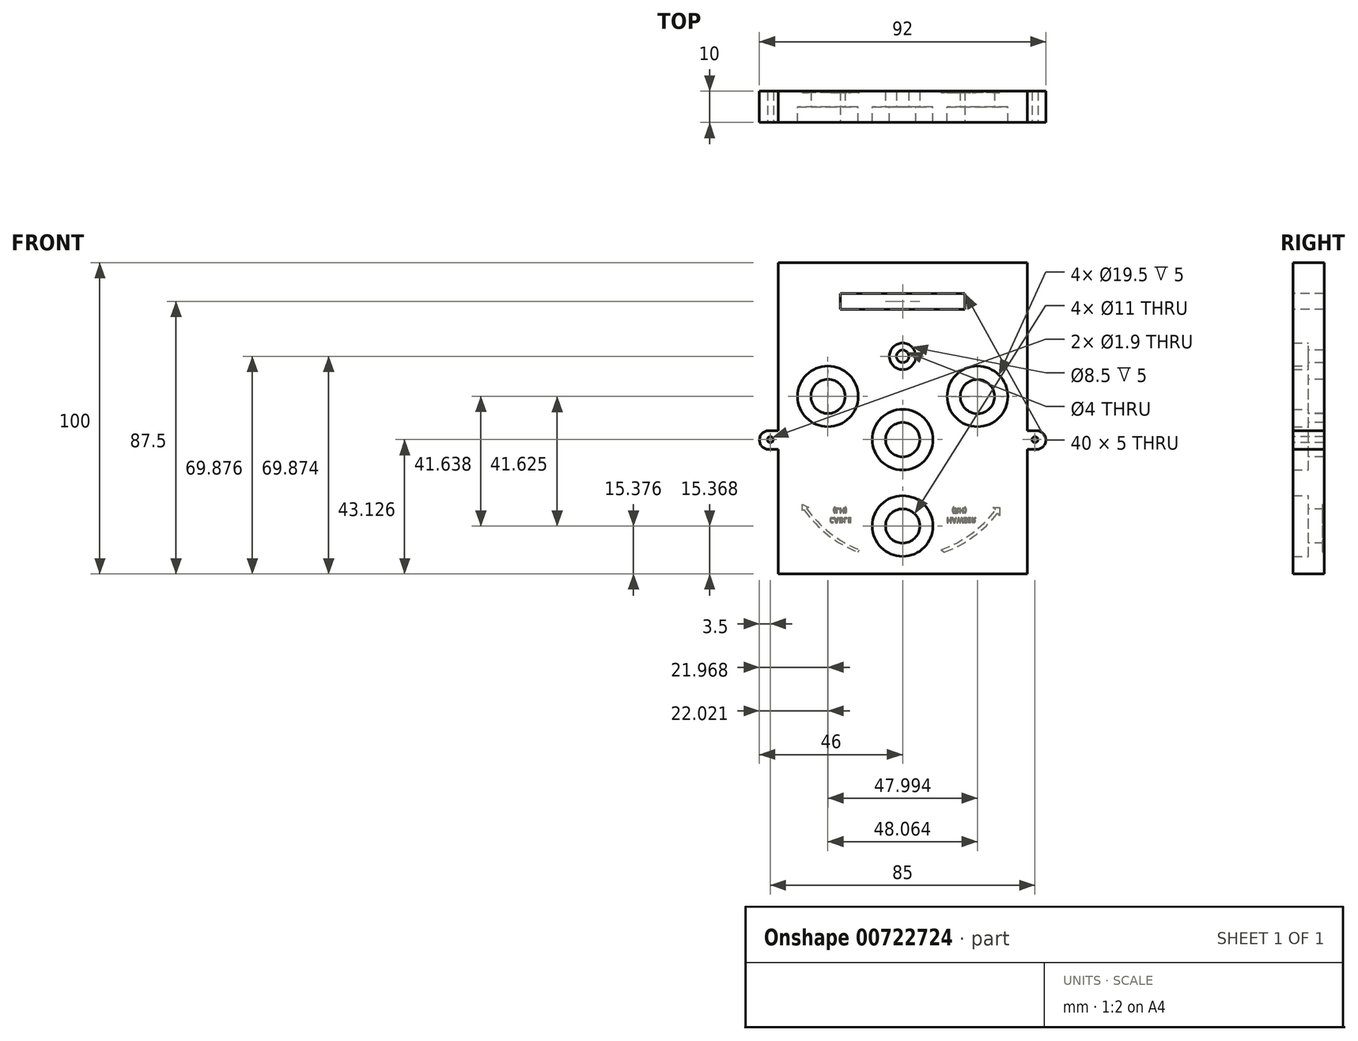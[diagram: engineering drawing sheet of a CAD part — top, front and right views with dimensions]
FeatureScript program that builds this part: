
annotation { "Feature Type Name" : "Feature", "Feature Type Description" : "" }
export const myFeature = defineFeature(function(context is Context, id is Id, definition is map)
    precondition{}
    {
        {
            var Q0;
            Q0=qCreatedBy(makeId("Front.planeOp"),FACE);
            var sketch = newSketch(context, id + "F0", { "sketchPlane" : qUnion([Q0])});
            skLineSegment(sketch, "E0.bottom", {"start": v(-40, 60) * mm, "end": v(40, 60) * mm});
            skLineSegment(sketch, "E0.top", {"start": v(-40, -60) * mm, "end": v(40, -60) * mm});
            skLineSegment(sketch, "E0.left", {"start": v(-40, 60) * mm, "end": v(-40, -60) * mm});
            skLineSegment(sketch, "E0.right", {"start": v(40, 60) * mm, "end": v(40, -60) * mm});
            skPoint(sketch, "E0.middle", {"position": v(0, 0) * mm});
            skLineSegment(sketch, "E1", {"start": v(0, 21.88) * mm, "end": v(0, 29.88) * mm, "construction": true});
            skCircle(sketch, "E2", {"center": v(0, 29.88) * mm, "radius": 8 * mm, "construction": true});
            skCircle(sketch, "E3", {"center": v(0, 29.88) * mm, "radius": 4.25 * mm});
            skLineSegment(sketch, "E4", {"start": v(0, 60) * mm, "end": v(0, 29.88) * mm, "construction": true});
            skLineSegment(sketch, "E5", {"start": v(0, 21.88) * mm, "end": v(0, 3.13) * mm, "construction": true});
            skCircle(sketch, "E6", {"center": v(0, 3.13) * mm, "radius": 18.75 * mm, "construction": true});
            skCircle(sketch, "E7.cCircle", {"center": v(0, 3.13) * mm, "radius": 27.75 * mm, "construction": true});
            skLineSegment(sketch, "E7.0", {"start": v(0, -24.62) * mm, "end": v(-24.03, 17) * mm, "construction": true});
            skLineSegment(sketch, "E7.1", {"start": v(-24.03, 17) * mm, "end": v(24.03, 17) * mm, "construction": true});
            skLineSegment(sketch, "E7.2", {"start": v(24.03, 17) * mm, "end": v(0, -24.62) * mm, "construction": true});
            skCircle(sketch, "E8", {"center": v(24.03, 17) * mm, "radius": 8 * mm, "construction": true});
            skCircle(sketch, "E9", {"center": v(-24.03, 17) * mm, "radius": 8 * mm, "construction": true});
            skCircle(sketch, "E10", {"center": v(0, -24.62) * mm, "radius": 8 * mm, "construction": true});
            skCircle(sketch, "E11", {"center": v(0, 3.13) * mm, "radius": 9.75 * mm});
            skCircle(sketch, "E12", {"center": v(24.03, 17) * mm, "radius": 9.75 * mm});
            skCircle(sketch, "E13", {"center": v(-24.03, 17) * mm, "radius": 9.75 * mm});
            skCircle(sketch, "E14", {"center": v(0, -24.62) * mm, "radius": 9.75 * mm});
            skSolve(sketch);
        }
        {
            var Q0;
            Q0=qSketchRegion(id+"F0",true);
            extrude(context, id + "F1", {"entities" : qUnion([Q0]), "depth" : 5 * mm, "offsetDistance" : 25 * mm});
        }
        {
            var Q0;
            Q0=qCreatedBy(makeId("Front.planeOp"),FACE);
            var sketch = newSketch(context, id + "F2", { "sketchPlane" : qUnion([Q0])});
            skLineSegment(sketch, "E15.bottom", {"start": v(40, -60) * mm, "end": v(-40, -60) * mm});
            skLineSegment(sketch, "E15.top", {"start": v(40, 60) * mm, "end": v(-40, 60) * mm});
            skLineSegment(sketch, "E15.left", {"start": v(40, -60) * mm, "end": v(40, 60) * mm});
            skLineSegment(sketch, "E15.right", {"start": v(-40, -60) * mm, "end": v(-40, 60) * mm});
            skPoint(sketch, "E15.middle", {"position": v(0, 0) * mm});
            skCircle(sketch, "E16", {"center": v(0, 3.12) * mm, "radius": 5.5 * mm});
            skCircle(sketch, "E17", {"center": v(0, -24.63) * mm, "radius": 5.5 * mm});
            skCircle(sketch, "E18", {"center": v(24.02, 16.94) * mm, "radius": 5.5 * mm});
            skCircle(sketch, "E19", {"center": v(-23.98, 17) * mm, "radius": 5.5 * mm});
            skCircle(sketch, "E20", {"center": v(0, 29.87) * mm, "radius": 2 * mm});
            skSolve(sketch);
        }
        {
            var Q0;
            Q0=qSketchRegion(id+"F2",true);
            extrude(context, id + "F3", {"entities" : qUnion([Q0]), "operationType" : NewBodyOperationType.ADD, "oppositeDirection" : true, "depth" : 5 * mm, "offsetDistance" : 25 * mm});
        }
        {
            var Q0;
            Q0=makeQuery(id+"F1.opExtrude","CAP_FACE",FACE,{"disambiguationData":[OSD([sQuery(id+"F0.wireOp",EDGE,"E0.bottom"),sQuery(id+"F0.wireOp",EDGE,"E0.top"),sQuery(id+"F0.wireOp",EDGE,"E0.left"),sQuery(id+"F0.wireOp",EDGE,"E0.right"),sQuery(id+"F0.wireOp",EDGE,"E11"),sQuery(id+"F0.wireOp",EDGE,"E3"),sQuery(id+"F0.wireOp",EDGE,"E12"),sQuery(id+"F0.wireOp",EDGE,"E13"),sQuery(id+"F0.wireOp",EDGE,"E14")])],"isStart":false});
            var sketch = newSketch(context, id + "F4", { "sketchPlane" : qUnion([Q0])});
            skLineSegment(sketch, "E21.bottom", {"start": v(40, -60) * mm, "end": v(-40, -60) * mm});
            skLineSegment(sketch, "E21.top", {"start": v(40, -40) * mm, "end": v(-40, -40) * mm});
            skLineSegment(sketch, "E21.left", {"start": v(40, -60) * mm, "end": v(40, -40) * mm});
            skLineSegment(sketch, "E21.right", {"start": v(-40, -60) * mm, "end": v(-40, -40) * mm});
            skSolve(sketch);
        }
        {
            var Q0;
            Q0=qSketchRegion(id+"F4",true);
            extrude(context, id + "F5", {"entities" : qUnion([Q0]), "operationType" : NewBodyOperationType.REMOVE, "oppositeDirection" : true, "depth" : 10 * mm, "offsetDistance" : 25 * mm});
        }
        {
            var Q0;
            Q0=makeQuery(id+"F1.opExtrude","CAP_FACE",FACE,{"disambiguationData":[OSD([sQuery(id+"F0.wireOp",EDGE,"E0.bottom"),sQuery(id+"F0.wireOp",EDGE,"E0.top"),sQuery(id+"F0.wireOp",EDGE,"E0.left"),sQuery(id+"F0.wireOp",EDGE,"E0.right"),sQuery(id+"F0.wireOp",EDGE,"E11"),sQuery(id+"F0.wireOp",EDGE,"E3"),sQuery(id+"F0.wireOp",EDGE,"E12"),sQuery(id+"F0.wireOp",EDGE,"E13"),sQuery(id+"F0.wireOp",EDGE,"E14")])],"isStart":false});
            var sketch = newSketch(context, id + "F6", { "sketchPlane" : qUnion([Q0])});
            skLineSegment(sketch, "E22", {"start": v(0, 3.13) * mm, "end": v(42.5, 3.13) * mm, "construction": true});
            skLineSegment(sketch, "E23", {"start": v(42.5, 3.13) * mm, "end": v(42.5, 0.13) * mm, "construction": true});
            skLineSegment(sketch, "E24.bottom", {"start": v(40, 0) * mm, "end": v(46, 0) * mm});
            skLineSegment(sketch, "E24.top", {"start": v(40, 6) * mm, "end": v(46, 6) * mm});
            skLineSegment(sketch, "E24.left", {"start": v(40, 0) * mm, "end": v(40, 6) * mm});
            skLineSegment(sketch, "E24.right", {"start": v(46, 0) * mm, "end": v(46, 6) * mm});
            skCircle(sketch, "E25", {"center": v(42.5, 3.13) * mm, "radius": 0.95 * mm});
            skSolve(sketch);
        }
        {
            var Q0;
            Q0=qSketchRegion(id+"F6",true);
            extrude(context, id + "F7", {"entities" : qUnion([Q0]), "oppositeDirection" : true, "depth" : 10 * mm, "offsetDistance" : 25 * mm});
        }
        {
            var Q0;
            Q0=makeQuery(id+"F7.opExtrude","SWEPT_EDGE",EDGE,{"disambiguationData":[OSD([sQuery(id+"F6.wireOp",EDGE,"E24.bottom"),sQuery(id+"F6.wireOp",EDGE,"E24.right")])]});
            var Q1;
            Q1=makeQuery(id+"F7.opExtrude","SWEPT_EDGE",EDGE,{"disambiguationData":[OSD([sQuery(id+"F6.wireOp",EDGE,"E24.top"),sQuery(id+"F6.wireOp",EDGE,"E24.right")])]});
            fillet(context, id + "F8", {"entities" : qUnion([Q0, Q1]), "radius" : 3 * mm, "tangentPropagation" : true, "allowEdgeOverflow" : false});
        }
        {
            var Q0;
            Q0=makeQuery(id+"F7.opExtrude","SWEPT_BODY",BODY,{"disambiguationData":[OSD([sQuery(id+"F6.wireOp",EDGE,"E24.bottom"),sQuery(id+"F6.wireOp",EDGE,"E24.top"),sQuery(id+"F6.wireOp",EDGE,"E24.left"),sQuery(id+"F6.wireOp",EDGE,"E24.right"),sQuery(id+"F6.wireOp",EDGE,"E25")])]});
            var Q1;
            Q1=qCreatedBy(makeId("Right.planeOp"),FACE);
            mirror(context, id + "F9", {"operationType" : NewBodyOperationType.ADD, "entities" : qUnion([Q0]), "mirrorPlane" : qUnion([Q1])});
        }
        {
            var Q0;
            Q0=makeQuery(id+"F1.opExtrude","CAP_FACE",FACE,{"disambiguationData":[OSD([sQuery(id+"F0.wireOp",EDGE,"E0.bottom"),sQuery(id+"F0.wireOp",EDGE,"E0.top"),sQuery(id+"F0.wireOp",EDGE,"E0.left"),sQuery(id+"F0.wireOp",EDGE,"E0.right"),sQuery(id+"F0.wireOp",EDGE,"BUhoPo5e-iJjO-Hz3U-B1AJ-PJeumMdkG3JQ"),sQuery(id+"F0.wireOp",EDGE,"E3"),sQuery(id+"F0.wireOp",EDGE,"iMyCUadU-kSq6-7gJk-bGzv-rUmCgOXwhL5P"),sQuery(id+"F0.wireOp",EDGE,"g6cQsEgE-VhaZ-rvnu-1JBG-t1yHCIxkASWM"),sQuery(id+"F0.wireOp",EDGE,"NTCEa5vw-s6QI-k5br-llQC-EMKQmXEYU9zL")])],"isStart":false});
            var sketch = newSketch(context, id + "F11", { "sketchPlane" : qUnion([Q0])});
            skLineSegment(sketch, "E26", {"start": v(40, 60) * mm, "end": v(20, 60) * mm, "construction": true});
            skLineSegment(sketch, "E27", {"start": v(20, 60) * mm, "end": v(20, 50) * mm, "construction": true});
            skLineSegment(sketch, "E28.bottom", {"start": v(20, 50) * mm, "end": v(-20, 50) * mm});
            skLineSegment(sketch, "E28.top", {"start": v(20, 45) * mm, "end": v(-20, 45) * mm});
            skLineSegment(sketch, "E28.left", {"start": v(20, 50) * mm, "end": v(20, 45) * mm});
            skLineSegment(sketch, "E28.right", {"start": v(-20, 50) * mm, "end": v(-20, 45) * mm});
            skSolve(sketch);
        }
        {
            var Q0;
            Q0=qSketchRegion(id+"F11",true);
            extrude(context, id + "F12", {"entities" : qUnion([Q0]), "operationType" : NewBodyOperationType.REMOVE, "oppositeDirection" : true, "depth" : 10 * mm, "offsetDistance" : 25 * mm, "hasSecondDirection" : true, "secondDirectionOppositeDirection" : false, "secondDirectionDepth" : 2 * mm});
        }
        {
            var Q0;
            {var subQ0=makeQuery(id+"F7.opExtrude","CAP_FACE",FACE,{"disambiguationData":[OSD([sQuery(id+"F6.wireOp",EDGE,"E24.bottom"),sQuery(id+"F6.wireOp",EDGE,"E24.top"),sQuery(id+"F6.wireOp",EDGE,"E24.left"),sQuery(id+"F6.wireOp",EDGE,"E24.right"),sQuery(id+"F6.wireOp",EDGE,"E25")])],"isStart":false});Q0=makeQuery(id+"F9.boolean.opBoolean","MERGE",FACE,{"derivedFrom":[makeQuery(id+"F3.opExtrude","CAP_FACE",FACE,{"disambiguationData":[OSD([sQuery(id+"F2.wireOp",EDGE,"E15.bottom"),sQuery(id+"F2.wireOp",EDGE,"E15.top"),sQuery(id+"F2.wireOp",EDGE,"E15.left"),sQuery(id+"F2.wireOp",EDGE,"E15.right"),sQuery(id+"F2.wireOp",EDGE,"E16"),sQuery(id+"F2.wireOp",EDGE,"E17"),sQuery(id+"F2.wireOp",EDGE,"E18"),sQuery(id+"F2.wireOp",EDGE,"E19"),sQuery(id+"F2.wireOp",EDGE,"E20")])],"isStart":false}),subQ0,makeQuery(id+"F9.opPattern","COPY",FACE,{"derivedFrom":subQ0,"instanceName":"1"})]});}
            var sketch = newSketch(context, id + "F13", { "sketchPlane" : qUnion([Q0])});
            skArc(sketch, "E29", {"start": v(14.26, -33.06) * mm, "mid": v(23.94, -27.53) * mm, "end": v(31.65, -19.48) * mm});
            skArc(sketch, "E30", {"start": v(13.93, -32.23) * mm, "mid": v(23.4, -26.82) * mm, "end": v(30.94, -18.94) * mm});
            skArc(sketch, "E31", {"start": v(-13.38, -33.06) * mm, "mid": v(-22.83, -27.98) * mm, "end": v(-30.51, -20.48) * mm});
            skArc(sketch, "E32", {"start": v(-12.33, -32.23) * mm, "mid": v(-22.03, -27.15) * mm, "end": v(-29.85, -19.48) * mm});
            skLineSegment(sketch, "E33", {"start": v(14.26, -33.06) * mm, "end": v(13.93, -32.23) * mm});
            skLineSegment(sketch, "E34", {"start": v(-12.33, -32.23) * mm, "end": v(-13.38, -33.06) * mm});
            skLineSegment(sketch, "E35.2", {"start": v(28.49, -20.51) * mm, "end": v(28.49, -20.51) * mm});
            skPoint(sketch, "E35.0.midPoint", {"position": v(31.65, -20.51) * mm});
            skPoint(sketch, "E35.cCircle.center.orphan", {"position": v(31.65, -18.69) * mm});
            skPoint(sketch, "E36.orphan", {"position": v(34.82, -20.51) * mm});
            skLineSegment(sketch, "E37", {"start": v(31.65, -19.48) * mm, "end": v(32.26, -19.73) * mm});
            skLineSegment(sketch, "E38", {"start": v(32.26, -19.73) * mm, "end": v(32.26, -17.7) * mm});
            skLineSegment(sketch, "E39", {"start": v(32.26, -17.7) * mm, "end": v(30.18, -18.62) * mm});
            skLineSegment(sketch, "E40", {"start": v(30.18, -18.62) * mm, "end": v(30.94, -18.94) * mm});
            skPoint(sketch, "E41.trimOffspring.end.orphan", {"position": v(31.65, -17.9) * mm});
            skLineSegment(sketch, "E42", {"start": v(-29.85, -19.48) * mm, "end": v(-29.05, -18.72) * mm});
            skLineSegment(sketch, "E43", {"start": v(-29.05, -18.72) * mm, "end": v(-31.2, -18.72) * mm});
            skLineSegment(sketch, "E44", {"start": v(-31.2, -18.72) * mm, "end": v(-31.2, -21.32) * mm});
            skLineSegment(sketch, "E45", {"start": v(-31.2, -21.32) * mm, "end": v(-30.51, -20.48) * mm});
            skSolve(sketch);
        }
        {
            var Q0;
            Q0 = qSketchRegion(id + "F13", true);
            extrude(context, id + "F14", {"entities" : qUnion([Q0]), "operationType" : NewBodyOperationType.REMOVE, "oppositeDirection" : true, "depth" : 0.4 * mm, "offsetDistance" : 25 * mm});
        }
        {
            var Q0;
            {var subQ0=makeQuery(id+"F7.opExtrude","CAP_FACE",FACE,{"disambiguationData":[OSD([sQuery(id+"F6.wireOp",EDGE,"E24.bottom"),sQuery(id+"F6.wireOp",EDGE,"E24.top"),sQuery(id+"F6.wireOp",EDGE,"E24.left"),sQuery(id+"F6.wireOp",EDGE,"E24.right"),sQuery(id+"F6.wireOp",EDGE,"E25")])],"isStart":false});Q0=makeQuery(id+"F9.boolean.opBoolean","MERGE",FACE,{"derivedFrom":[makeQuery(id+"F3.opExtrude","CAP_FACE",FACE,{"disambiguationData":[OSD([sQuery(id+"F2.wireOp",EDGE,"E15.bottom"),sQuery(id+"F2.wireOp",EDGE,"E15.top"),sQuery(id+"F2.wireOp",EDGE,"E15.left"),sQuery(id+"F2.wireOp",EDGE,"E15.right"),sQuery(id+"F2.wireOp",EDGE,"E16"),sQuery(id+"F2.wireOp",EDGE,"E17"),sQuery(id+"F2.wireOp",EDGE,"E18"),sQuery(id+"F2.wireOp",EDGE,"E19"),sQuery(id+"F2.wireOp",EDGE,"E20")])],"isStart":false}),subQ0,makeQuery(id+"F9.opPattern","COPY",FACE,{"derivedFrom":subQ0,"instanceName":"1"})]});}
            var sketch = newSketch(context, id + "F15", { "sketchPlane" : qUnion([Q0])});
            skText(sketch, "E46", { "text": "HAWSER\n   (RH)", "fontName": "OpenSans-Bold.ttf"});
            skText(sketch, "E47", { "text": "CABLE\n  (LH)", "fontName": "OpenSans-Bold.ttf"});
            const initialGuessF15  = {"E46": [-0.0141, -0.02198, -0.99999, 0.00519, 0.00162], "E47": [0.02352, -0.02197, -0.99999, 0.00519, 0.00162]};
            skSetInitialGuess(sketch, initialGuessF15);
            skSolve(sketch);
        }
        {
            var Q0;
            Q0 = qSketchRegion(id + "F15", true);
            extrude(context, id + "F16", {"entities" : qUnion([Q0]), "operationType" : NewBodyOperationType.REMOVE, "oppositeDirection" : true, "depth" : 0.4 * mm, "offsetDistance" : 25 * mm});
        }
    });
